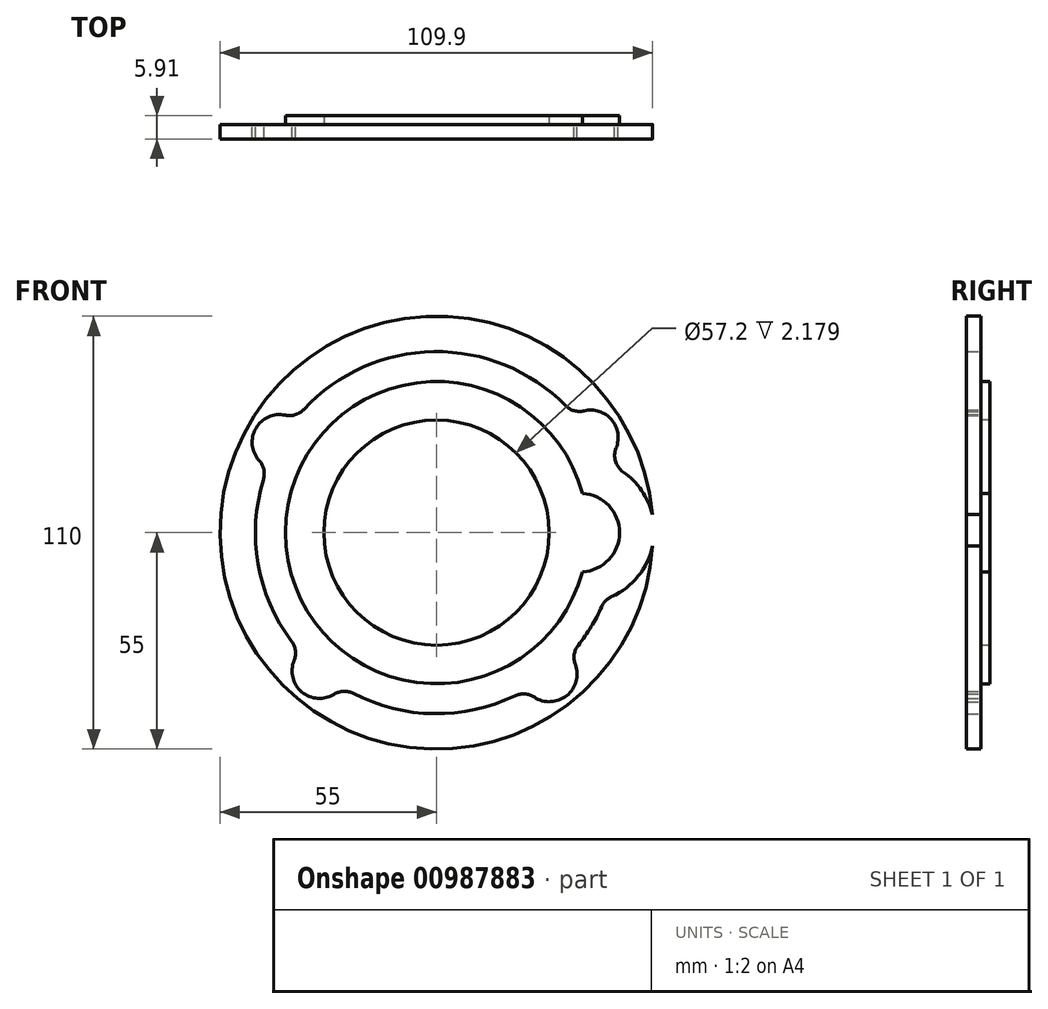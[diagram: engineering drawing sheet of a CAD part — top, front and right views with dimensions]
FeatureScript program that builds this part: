
annotation { "Feature Type Name" : "Feature", "Feature Type Description" : "" }
export const myFeature = defineFeature(function(context is Context, id is Id, definition is map)
    precondition{}
    {
        {
            var Q0;
            Q0=qCreatedBy(makeId("Right.planeOp"),FACE);
            var sketch = newSketch(context, id + "F0", { "sketchPlane" : qUnion([Q0])});
            skLineSegment(sketch, "E0", {"start": v(-36.46, 0) * mm, "end": v(47.74, 0) * mm, "construction": true});
            skLineSegment(sketch, "E1", {"start": v(0, 28.6) * mm, "end": v(0, 55) * mm});
            skLineSegment(sketch, "E2", {"start": v(-8, 39) * mm, "end": v(-8, 39) * mm});
            skLineSegment(sketch, "E3", {"start": v(0, 55) * mm, "end": v(-3, 55) * mm});
            skLineSegment(sketch, "E4", {"start": v(-8, 39) * mm, "end": v(-8, 50) * mm});
            skLineSegment(sketch, "E5", {"start": v(-8, 39) * mm, "end": v(-8, 25) * mm});
            skLineSegment(sketch, "E6", {"start": v(-31, 8.82) * mm, "end": v(-8, 8.82) * mm});
            skLineSegment(sketch, "E7", {"start": v(-31, 8.82) * mm, "end": v(-31, 4.06) * mm});
            skLineSegment(sketch, "E8.top", {"start": v(-31, 0) * mm, "end": v(-35, 0) * mm});
            skLineSegment(sketch, "E8.left", {"start": v(-31, 8.82) * mm, "end": v(-31, 0) * mm});
            skLineSegment(sketch, "E8.right", {"start": v(-35, 8.45) * mm, "end": v(-35, 0) * mm});
            skLineSegment(sketch, "E9", {"start": v(0, 38.4) * mm, "end": v(9.5, 38.4) * mm});
            skLineSegment(sketch, "E10", {"start": v(9.5, 38.4) * mm, "end": v(9.5, 28.6) * mm});
            skLineSegment(sketch, "E11", {"start": v(0, 28.6) * mm, "end": v(9.5, 28.6) * mm});
            skLineSegment(sketch, "E12", {"start": v(0, 28.6) * mm, "end": v(0, 15.2) * mm});
            skLineSegment(sketch, "E13", {"start": v(-8, 15.2) * mm, "end": v(0, 15.2) * mm});
            skLineSegment(sketch, "E14", {"start": v(-8, 15.2) * mm, "end": v(-8, 8.82) * mm});
            skLineSegment(sketch, "E15", {"start": v(-8, 8.82) * mm, "end": v(-8, 8.82) * mm});
            skLineSegment(sketch, "E16", {"start": v(-11.35, 20.28) * mm, "end": v(-31.65, 13.17) * mm});
            skPoint(sketch, "E17.visualSharp", {"position": v(-35, 12) * mm});
            skArc(sketch, "E17.filletArc", {"start": v(-31.65, 13.17) * mm, "mid": v(-34.08, 11.35) * mm, "end": v(-35, 8.45) * mm});
            skPoint(sketch, "E18.visualSharp", {"position": v(-8, 21.45) * mm});
            skArc(sketch, "E18.filletArc", {"start": v(-11.35, 20.28) * mm, "mid": v(-8.92, 22.1) * mm, "end": v(-8, 25) * mm});
            skPoint(sketch, "E19.visualSharp", {"position": v(-8, 55) * mm});
            skLineSegment(sketch, "E20", {"start": v(-3, 55) * mm, "end": v(-8, 55) * mm});
            skLineSegment(sketch, "E21", {"start": v(-8, 50) * mm, "end": v(-8, 55) * mm});
            skLineSegment(sketch, "E22", {"start": v(-8, 25) * mm, "end": v(-8, 15.2) * mm});
            skSolve(sketch);
        }
        {
            var Q0;
            {var subQ0=sQuery(id+"F0.wireOp",EDGE,"E3");Q0=makeQuery(id+"F0.imprint","IMPRINT",FACE,{"disambiguationData":[TD([[makeQuery(id+"F0.imprint","IMPRINT",EDGE,{"derivedFrom":subQ0}),1.0]])]});}
            var Q1;
            {var subQ2=sQuery(id+"F0.wireOp",EDGE,"E9");Q1=makeQuery(id+"F0.imprint","IMPRINT",FACE,{"disambiguationData":[TD([[makeQuery(id+"F0.imprint","IMPRINT",EDGE,{"derivedFrom":subQ2}),-1.0]])]});}
            var Q2;
            Q2=sQuery(id+"F0.wireOp",EDGE,"E0");
            revolve(context, id + "F1", {"surfaceOperationType" : NewSurfaceOperationType.NEW, "entities" : qUnion([Q0, Q1]), "axis" : qUnion([Q2]), "revolveType" : RevolveType.FULL});
        }
        {
            var Q0;
            Q0=makeQuery(id+"F1.opRevolve","SWEPT_FACE",FACE,{"disambiguationData":[OSD([sQuery(id+"F0.wireOp",EDGE,"E1")])]});
            var sketch = newSketch(context, id + "F2", { "sketchPlane" : qUnion([Q0])});
            skArc(sketch, "E23", {"start": v(33.68, 31.33) * mm, "mid": v(0.67, 46) * mm, "end": v(-32.76, 32.3) * mm, "construction": true});
            skCircle(sketch, "E24", {"center": v(39.84, 23) * mm, "radius": 3.5 * mm});
            skCircle(sketch, "E25", {"center": v(-28.7, -35.95) * mm, "radius": 3.5 * mm});
            skArc(sketch, "E26", {"start": v(-37.5, 30.95) * mm, "mid": v(-44.47, 28.7) * mm, "end": v(-45.63, 21.48) * mm});
            skArc(sketch, "E27", {"start": v(45.04, 18.32) * mm, "mid": v(45.9, 26.5) * mm, "end": v(38.38, 29.85) * mm});
            skArc(sketch, "E28.trimOffspring", {"start": v(33.68, 31.33) * mm, "mid": v(0.67, 46) * mm, "end": v(-32.76, 32.3) * mm});
            skPoint(sketch, "E29.visualSharp", {"position": v(-35.04, 29.8) * mm});
            skArc(sketch, "E29.filletArc", {"start": v(-37.5, 30.95) * mm, "mid": v(-34.95, 31) * mm, "end": v(-32.76, 32.3) * mm});
            skArc(sketch, "E30", {"start": v(26.02, -41.07) * mm, "mid": v(34.22, -40.47) * mm, "end": v(36.18, -32.48) * mm});
            skArc(sketch, "E31.trimOffspring", {"start": v(36.81, -27.59) * mm, "mid": v(45.32, -7.9) * mm, "end": v(43.97, 13.5) * mm, "construction": true});
            skArc(sketch, "E32.trimOffspring", {"start": v(36.81, -27.59) * mm, "mid": v(45.32, -7.9) * mm, "end": v(43.97, 13.5) * mm});
            skArc(sketch, "E33", {"start": v(-35.25, -33.49) * mm, "mid": v(-33.06, -41.42) * mm, "end": v(-24.84, -41.8) * mm});
            skArc(sketch, "E34.trimOffspring", {"start": v(-19.92, -41.46) * mm, "mid": v(0.65, -46) * mm, "end": v(21.1, -40.88) * mm, "construction": true});
            skArc(sketch, "E35.trimOffspring", {"start": v(-19.92, -41.46) * mm, "mid": v(0.65, -46) * mm, "end": v(21.1, -40.88) * mm});
            skArc(sketch, "E36.trimOffspring", {"start": v(-42, -18.78) * mm, "mid": v(-39.31, -23.89) * mm, "end": v(-36.01, -28.62) * mm});
            skLineSegment(sketch, "E37", {"start": v(0, 0) * mm, "end": v(-64.26, 0) * mm, "construction": true});
            skLineSegment(sketch, "E38", {"start": v(-37, 0) * mm, "end": v(-37, 0.42) * mm, "construction": true});
            skArc(sketch, "E39", {"start": v(-47.4, 15.46) * mm, "mid": v(-55.21, -1.25) * mm, "end": v(-44.5, -16.26) * mm});
            skArc(sketch, "E40.filletArc", {"start": v(-47.4, 15.46) * mm, "mid": v(-45.45, 18.15) * mm, "end": v(-45.63, 21.48) * mm});
            skPoint(sketch, "E41.orphan", {"position": v(-37, 5.3) * mm});
            skPoint(sketch, "E42.orphan", {"position": v(-37, -4.46) * mm});
            skPoint(sketch, "E43.visualSharp", {"position": v(-33.82, -31.18) * mm});
            skArc(sketch, "E43.filletArc", {"start": v(-35.25, -33.49) * mm, "mid": v(-34.99, -30.95) * mm, "end": v(-36.01, -28.62) * mm});
            skPoint(sketch, "E44.visualSharp", {"position": v(-42.77, -16.94) * mm});
            skArc(sketch, "E44.filletArc", {"start": v(-42, -18.78) * mm, "mid": v(-43.02, -17.29) * mm, "end": v(-44.5, -16.26) * mm});
            skPoint(sketch, "E45.visualSharp", {"position": v(-22.9, -39.9) * mm});
            skArc(sketch, "E45.filletArc", {"start": v(-19.92, -41.46) * mm, "mid": v(-22.42, -40.98) * mm, "end": v(-24.84, -41.8) * mm});
            skPoint(sketch, "E46.visualSharp", {"position": v(24.03, -39.22) * mm});
            skArc(sketch, "E46.filletArc", {"start": v(26.02, -41.07) * mm, "mid": v(23.58, -40.33) * mm, "end": v(21.1, -40.88) * mm});
            skPoint(sketch, "E47.visualSharp", {"position": v(34.69, -30.2) * mm});
            skArc(sketch, "E47.filletArc", {"start": v(36.81, -27.59) * mm, "mid": v(35.85, -29.95) * mm, "end": v(36.18, -32.48) * mm});
            skArc(sketch, "E48.filletArc", {"start": v(45.04, 18.32) * mm, "mid": v(43.87, 16.05) * mm, "end": v(43.97, 13.5) * mm});
            skPoint(sketch, "E49.visualSharp", {"position": v(35.89, 28.78) * mm});
            skArc(sketch, "E49.filletArc", {"start": v(33.68, 31.33) * mm, "mid": v(35.83, 29.97) * mm, "end": v(38.38, 29.85) * mm});
            skLineSegment(sketch, "E50", {"start": v(29.7, -35.12) * mm, "end": v(30.4, -35.12) * mm, "construction": true});
            skCircle(sketch, "E51", {"center": v(30.4, -35.12) * mm, "radius": 3.5 * mm});
            skLineSegment(sketch, "E52.trimOffspring", {"start": v(33.9, -35.12) * mm, "end": v(36.2, -35.12) * mm, "construction": true});
            skLineSegment(sketch, "E53", {"start": v(-39.15, 24.14) * mm, "end": v(-47.83, 24.14) * mm, "construction": true});
            skLineSegment(sketch, "E54", {"start": v(-39.15, 24.14) * mm, "end": v(-39.15, 30.05) * mm, "construction": true});
            skLineSegment(sketch, "E55", {"start": v(-37.18, 23.4) * mm, "end": v(-45.42, 23.4) * mm, "construction": true});
            skLineSegment(sketch, "E56", {"start": v(-39.55, 29.48) * mm, "end": v(-39.55, 20.14) * mm, "construction": true});
            skCircle(sketch, "E57", {"center": v(-39.55, 23.4) * mm, "radius": 3.5 * mm});
            skLineSegment(sketch, "E58", {"start": v(22.75, 26.15) * mm, "end": v(-22.56, 26.15) * mm, "construction": true});
            skSolve(sketch);
        }
        {
            var Q0;
            Q0=makeQuery(id+"F2.imprint","IMPRINT",FACE,{"disambiguationData":[TD([[makeQuery(id+"F2.imprint","IMPRINT",EDGE,{"derivedFrom":sQuery(id+"F2.wireOp",EDGE,"E25")}),1.0]])]});
            var Q1;
            Q1=makeQuery(id+"F2.imprint","IMPRINT",FACE,{"disambiguationData":[TD([[makeQuery(id+"F2.imprint","IMPRINT",EDGE,{"derivedFrom":sQuery(id+"F2.wireOp",EDGE,"vF8NlBrY-gT3t-dSrl-N8A3-qaZWvNv37Ga3")}),1.0]])]});
            var Q2;
            Q2=makeQuery(id+"F2.imprint","IMPRINT",FACE,{"disambiguationData":[TD([[makeQuery(id+"F2.imprint","IMPRINT",EDGE,{"derivedFrom":sQuery(id+"F2.wireOp",EDGE,"qRvUgUbT-ozD9-ka05-iYK2-iiEVyybRubCF")}),1.0]])]});
            var Q3;
            Q3=makeQuery(id+"F2.imprint","IMPRINT",FACE,{"disambiguationData":[TD([[makeQuery(id+"F2.imprint","IMPRINT",EDGE,{"derivedFrom":sQuery(id+"F2.wireOp",EDGE,"E24")}),1.0]])]});
            var Q4;
            Q4=makeQuery(id+"F2.imprint","IMPRINT",FACE,{"disambiguationData":[TD([[makeQuery(id+"F2.imprint","IMPRINT",EDGE,{"derivedFrom":sQuery(id+"F2.wireOp",EDGE,"E51")}),1.0]])]});
            var Q5;
            Q5=makeQuery(id+"F2.imprint","IMPRINT",FACE,{"disambiguationData":[TD([[makeQuery(id+"F2.imprint","IMPRINT",EDGE,{"derivedFrom":sQuery(id+"F2.wireOp",EDGE,"E57")}),1.0]])]});
            extrude(context, id + "F3", {"entities" : qUnion([Q0, Q1, Q2, Q3, Q4, Q5]), "operationType" : NewBodyOperationType.REMOVE, "oppositeDirection" : true, "depth" : 25 * mm, "offsetDistance" : 25 * mm});
        }
        {
            var Q0;
            Q0=makeQuery(id+"F1.opRevolve","SWEPT_FACE",FACE,{"disambiguationData":[OSD([sQuery(id+"F0.wireOp",EDGE,"E10")])]});
            var sketch = newSketch(context, id + "F4", { "sketchPlane" : qUnion([Q0])});
            skArc(sketch, "E59", {"start": v(-36.42, 10) * mm, "mid": v(-46.5, 0) * mm, "end": v(-36.42, -10) * mm});
            skArc(sketch, "E60", {"start": v(-36.42, -10) * mm, "mid": v(37.76, 0) * mm, "end": v(-36.42, 10) * mm});
            skSolve(sketch);
        }
        {
            var Q0;
            {var subQ0=sQuery(id+"F4.wireOp",EDGE,"E59");var subQ1=makeQuery(id+"F1.opRevolve","SWEPT_EDGE",EDGE,{"disambiguationData":[OSD([sQuery(id+"F0.wireOp",EDGE,"E9"),sQuery(id+"F0.wireOp",EDGE,"E10")])]});var subQ2=makeQuery(id+"F4.imprint","INTERSECT",VERTEX,{"disambiguationData":[OD(0.0)],"derivedFrom":[subQ1,subQ0]});Q0=makeQuery(id+"F4.imprint","IMPRINT",FACE,{"disambiguationData":[TD([[makeQuery(id+"F4.imprint","IMPRINT",EDGE,{"disambiguationData":[TD([[subQ2,-1.0]])],"derivedFrom":subQ0}),1.0]])]});}
            var Q1;
            {var subQ0=sQuery(id+"F4.wireOp",EDGE,"mHmDqNqn-Vxvk-4JxU-M1xk-mwOj1SqFVGgA");var subQ1=makeQuery(id+"F1.opRevolve","SWEPT_EDGE",EDGE,{"disambiguationData":[OSD([sQuery(id+"F0.wireOp",EDGE,"E9"),sQuery(id+"F0.wireOp",EDGE,"E10")])]});var subQ2=makeQuery(id+"F4.imprint","INTERSECT",VERTEX,{"disambiguationData":[OD(0.0)],"derivedFrom":[subQ1,subQ0]});Q1=makeQuery(id+"F4.imprint","IMPRINT",FACE,{"disambiguationData":[TD([[makeQuery(id+"F4.imprint","IMPRINT",EDGE,{"disambiguationData":[TD([[subQ2,1.0]])],"derivedFrom":subQ0}),1.0]])]});}
            var Q2;
            {var subQ0=sQuery(id+"F4.wireOp",EDGE,"mHmDqNqn-Vxvk-4JxU-M1xk-mwOj1SqFVGgA");var subQ1=makeQuery(id+"F1.opRevolve","SWEPT_EDGE",EDGE,{"disambiguationData":[OSD([sQuery(id+"F0.wireOp",EDGE,"E9"),sQuery(id+"F0.wireOp",EDGE,"E10")])]});var subQ2=makeQuery(id+"F4.imprint","INTERSECT",VERTEX,{"disambiguationData":[OD(0.0)],"derivedFrom":[subQ1,subQ0]});Q2=makeQuery(id+"F4.imprint","IMPRINT",FACE,{"disambiguationData":[TD([[makeQuery(id+"F4.imprint","IMPRINT",EDGE,{"disambiguationData":[TD([[subQ2,-1.0]])],"derivedFrom":subQ0}),1.0]])]});}
            extrude(context, id + "F5", {"entities" : qUnion([Q0, Q1, Q2]), "oppositeDirection" : true, "depth" : 10 * mm, "offsetDistance" : 25 * mm});
        }
        {
            var Q0;
            Q0=makeQuery(id+"F1.opRevolve","SWEPT_BODY",BODY,{"disambiguationData":[OSD([sQuery(id+"F0.wireOp",EDGE,"E1"),sQuery(id+"F0.wireOp",EDGE,"E3"),sQuery(id+"F0.wireOp",EDGE,"E4"),sQuery(id+"F0.wireOp",EDGE,"E5"),sQuery(id+"F0.wireOp",EDGE,"E6"),sQuery(id+"F0.wireOp",EDGE,"E8.top"),sQuery(id+"F0.wireOp",EDGE,"E8.left"),sQuery(id+"F0.wireOp",EDGE,"E8.right"),sQuery(id+"F0.wireOp",EDGE,"E9"),sQuery(id+"F0.wireOp",EDGE,"E10"),sQuery(id+"F0.wireOp",EDGE,"E11"),sQuery(id+"F0.wireOp",EDGE,"E12"),sQuery(id+"F0.wireOp",EDGE,"E13"),sQuery(id+"F0.wireOp",EDGE,"E14"),sQuery(id+"F0.wireOp",EDGE,"E16"),sQuery(id+"F0.wireOp",EDGE,"E17.filletArc"),sQuery(id+"F0.wireOp",EDGE,"E18.filletArc"),sQuery(id+"F0.wireOp",EDGE,"E19.filletArc")])]});
            var Q1;
            Q1=makeQuery(id+"F5.opExtrude","SWEPT_BODY",BODY,{"disambiguationData":[OSD([sQuery(id+"F0.wireOp",EDGE,"E10"),sQuery(id+"F0.wireOp",EDGE,"E11"),sQuery(id+"F4.wireOp",EDGE,"E59"),sQuery(id+"F4.wireOp",EDGE,"mHmDqNqn-Vxvk-4JxU-M1xk-mwOj1SqFVGgA"),sQuery(id+"F4.wireOp",EDGE,"3VAelAmh-KZIr-sE4I-JIhv-fC48lwr0Q9Bp"),sQuery(id+"F4.wireOp",EDGE,"261cf710-738f-4d8d-b37c-07c8346ab8f7.trimOffspring")])]});
            booleanBodies(context, id + "F6", {"operationType" : BooleanOperationType.UNION, "tools" : qUnion([Q0, Q1])});
        }
        {
            var Q0;
            Q0=makeQuery(id+"F6.opBoolean","SPLIT",EDGE,{"disambiguationData":[OD(1.0)],"derivedFrom":makeQuery(id+"F1.opRevolve","SWEPT_EDGE",EDGE,{"disambiguationData":[OSD([sQuery(id+"F0.wireOp",EDGE,"E9"),sQuery(id+"F0.wireOp",EDGE,"E10")])]})});
            var Q1;
            Q1=makeQuery(id+"F5.opExtrude","CAP_EDGE",EDGE,{"disambiguationData":[OSD([sQuery(id+"F4.wireOp",EDGE,"E59")])],"isStart":true});
            var Q2;
            Q2=makeQuery(id+"F6.opBoolean","SPLIT",EDGE,{"disambiguationData":[OD(0.0)],"derivedFrom":makeQuery(id+"F1.opRevolve","SWEPT_EDGE",EDGE,{"disambiguationData":[OSD([sQuery(id+"F0.wireOp",EDGE,"E9"),sQuery(id+"F0.wireOp",EDGE,"E10")])]})});
            var Q3;
            Q3=makeQuery(id+"F5.opExtrude","CAP_EDGE",EDGE,{"disambiguationData":[OSD([sQuery(id+"F4.wireOp",EDGE,"mHmDqNqn-Vxvk-4JxU-M1xk-mwOj1SqFVGgA")])],"isStart":true});
            chamfer(context, id + "F7", {"entities" : qUnion([Q0, Q1, Q2, Q3]), "width" : 2 * mm, "tangentPropagation" : true});
        }
        {
            var Q0;
            Q0 = qSketchRegion(id + "F2", true);
            extrude(context, id + "F8", {"entities" : qUnion([Q0]), "operationType" : NewBodyOperationType.REMOVE, "oppositeDirection" : true, "depth" : 25 * mm, "offsetDistance" : 25 * mm});
        }
        {
            var Q0;
            Q0=makeQuery(id+"F1.opRevolve","SWEPT_FACE",FACE,{"disambiguationData":[OSD([sQuery(id+"F0.wireOp",EDGE,"E4"),sQuery(id+"F0.wireOp",EDGE,"E5"),sQuery(id+"F0.wireOp",EDGE,"E21")])]});
            var sketch = newSketch(context, id + "F9", { "sketchPlane" : qUnion([Q0])});
            skCircle(sketch, "E61", {"center": v(28.7, -35.95) * mm, "radius": 5 * mm});
            skCircle(sketch, "E62", {"center": v(-39.84, 23) * mm, "radius": 5 * mm});
            skSolve(sketch);
        }
        {
            var Q0;
            Q0=makeQuery(id+"F9.imprint","IMPRINT",FACE,{"disambiguationData":[TD([[makeQuery(id+"F9.imprint","IMPRINT",EDGE,{"derivedFrom":sQuery(id+"F9.wireOp",EDGE,"E62")}),1.0]])]});
            var Q1;
            Q1=makeQuery(id+"F9.imprint","IMPRINT",FACE,{"disambiguationData":[TD([[makeQuery(id+"F9.imprint","IMPRINT",EDGE,{"derivedFrom":sQuery(id+"F9.wireOp",EDGE,"E62")}),1.0]])]});
            var Q2;
            Q2=makeQuery(id+"F9.imprint","IMPRINT",FACE,{"disambiguationData":[TD([[makeQuery(id+"F9.imprint","IMPRINT",EDGE,{"derivedFrom":sQuery(id+"F9.wireOp",EDGE,"E61")}),1.0]])]});
            var Q3;
            Q3=makeQuery(id+"F9.imprint","IMPRINT",FACE,{"disambiguationData":[TD([[makeQuery(id+"F9.imprint","IMPRINT",EDGE,{"derivedFrom":sQuery(id+"F9.wireOp",EDGE,"E62")}),1.0]])]});
            extrude(context, id + "F10", {"entities" : qUnion([Q0, Q1, Q2, Q3]), "operationType" : NewBodyOperationType.REMOVE, "oppositeDirection" : true, "depth" : 6 * mm, "offsetDistance" : 25 * mm});
        }
        {
            var Q0;
            Q0=qCreatedBy(makeId("Top.planeOp"),FACE);
            var sketch = newSketch(context, id + "F11", { "sketchPlane" : qUnion([Q0])});
            skLineSegment(sketch, "E63.bottom", {"start": v(-58.92, -3.73) * mm, "end": v(63.82, -3.73) * mm});
            skLineSegment(sketch, "E63.top", {"start": v(-58.92, -12.93) * mm, "end": v(63.82, -12.93) * mm});
            skLineSegment(sketch, "E63.left", {"start": v(-58.92, -3.73) * mm, "end": v(-58.92, -12.93) * mm});
            skLineSegment(sketch, "E63.right", {"start": v(63.82, -3.73) * mm, "end": v(63.82, -12.93) * mm});
            skLineSegment(sketch, "E64.bottom", {"start": v(-57.87, 2.18) * mm, "end": v(60.28, 2.18) * mm});
            skLineSegment(sketch, "E64.top", {"start": v(-57.87, 13.9) * mm, "end": v(60.28, 13.9) * mm});
            skLineSegment(sketch, "E64.left", {"start": v(-57.87, 2.18) * mm, "end": v(-57.87, 13.9) * mm});
            skLineSegment(sketch, "E64.right", {"start": v(60.28, 2.18) * mm, "end": v(60.28, 13.9) * mm});
            skSolve(sketch);
        }
        {
            var Q0;
            Q0=makeQuery(id+"F11.imprint","IMPRINT",FACE,{"disambiguationData":[TD([[makeQuery(id+"F11.imprint","IMPRINT",EDGE,{"derivedFrom":sQuery(id+"F11.wireOp",EDGE,"E63.bottom")}),-1.0]])]});
            var Q1;
            Q1=makeQuery(id+"F11.imprint","IMPRINT",FACE,{"disambiguationData":[TD([[makeQuery(id+"F11.imprint","IMPRINT",EDGE,{"derivedFrom":sQuery(id+"F11.wireOp",EDGE,"E64.bottom")}),1.0]])]});
            extrude(context, id + "F12", {"entities" : qUnion([Q0, Q1]), "operationType" : NewBodyOperationType.REMOVE, "oppositeDirection" : true, "depth" : 75.5 * mm, "offsetDistance" : 25 * mm, "hasSecondDirection" : true, "secondDirectionOppositeDirection" : false, "secondDirectionDepth" : 118.2 * mm});
        }
    });
